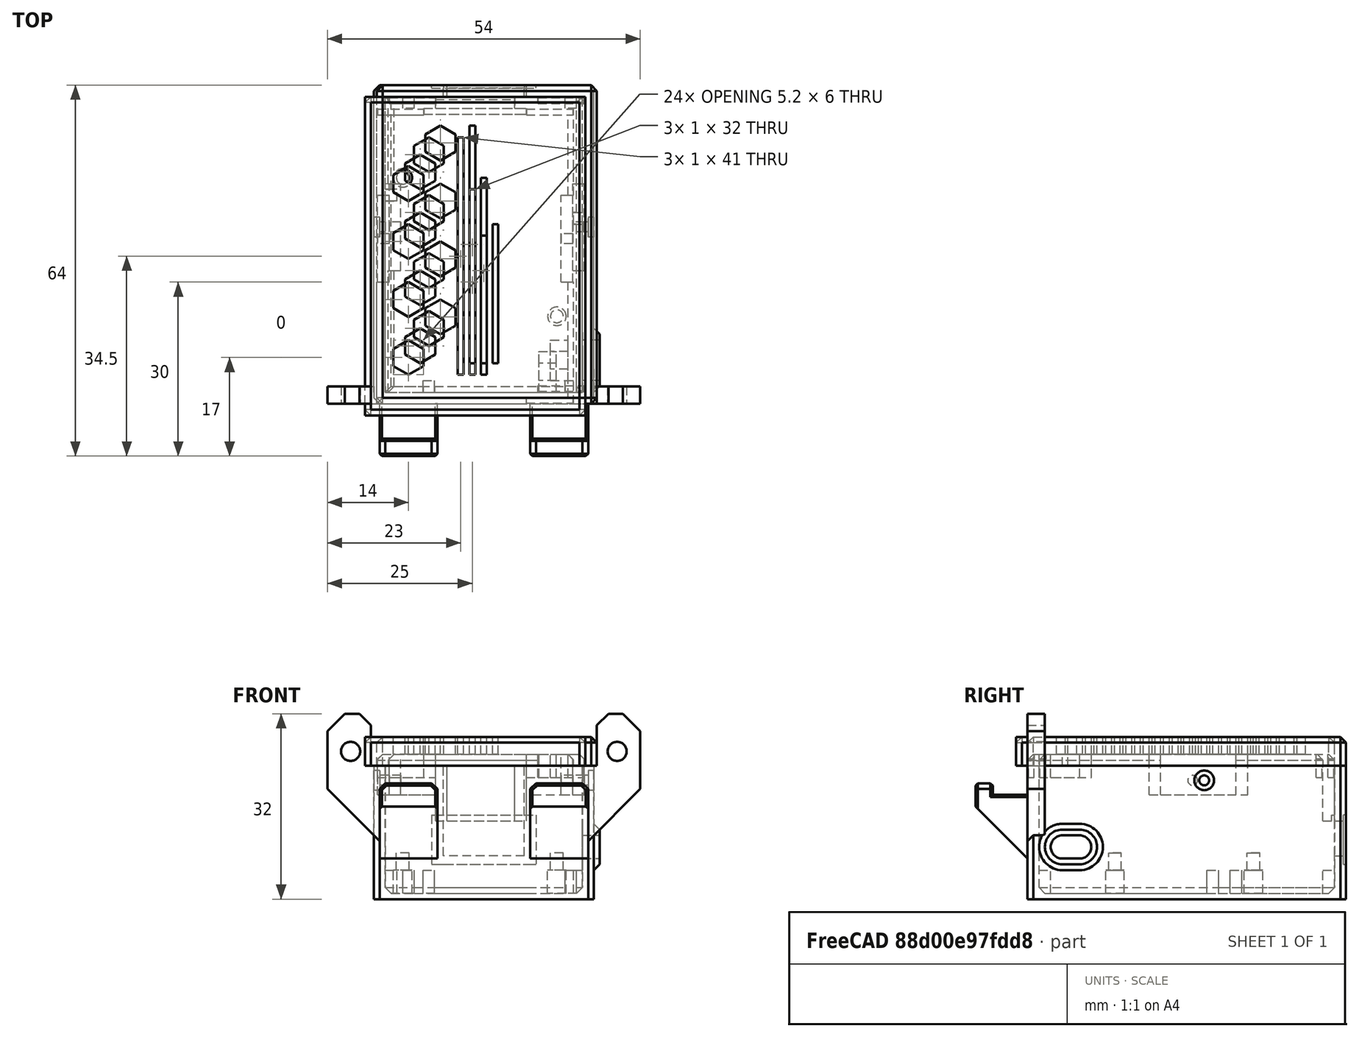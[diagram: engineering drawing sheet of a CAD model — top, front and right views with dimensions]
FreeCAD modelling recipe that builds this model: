
FCSTD DOCUMENT  (FreeCAD 0.18R16146 (Git))
Label: ac-dc5v-adapter
License: All rights reserved
LicenseURL: http://en.wikipedia.org/wiki/All_rights_reserved
objects: Part::Box×43, Part::MultiFuse×24, Part::Cylinder×15, Part::Chamfer×13, Part::Cut×12, Part::Feature×12
note: 119 computed .brp shape members not serialized (recipe doc carries the construction recipe); baked Part::Feature solids carry a one-line shape summary decoded from their .brp

FEATURE [Part::Box] Box  label="Cube"
  AttacherType = Attacher::AttachEngine3D
  Height = 1
  Length = 34
  Width = 51
FEATURE [Part::Box] Box001  label="Cube001"
  AttacherType = Attacher::AttachEngine3D
  Height = 5
  Length = 2
  Placement = pos=(6.5,0,0) rot=(0,0,1;0rad)
  Width = 2
FEATURE [Part::Box] Box002  label="Cube002"
  AttacherType = Attacher::AttachEngine3D
  Height = 5
  Length = 2
  Placement = pos=(0,33,0) rot=(0,0,1;0rad)
  Width = 2
FEATURE [Part::Box] Box003  label="Cube003"
  AttacherType = Attacher::AttachEngine3D
  Height = 5
  Length = 2
  Placement = pos=(31,0,0) rot=(0,0,1;0rad)
  Width = 2
FEATURE [Part::Box] Box004  label="Cube004"
  AttacherType = Attacher::AttachEngine3D
  Height = 5
  Length = 2
  Placement = pos=(31,49,0) rot=(0,0,1;0rad)
  Width = 2
FEATURE [Part::Box] Box005  label="Cube005"
  AttacherType = Attacher::AttachEngine3D
  Height = 5
  Length = 2
  Placement = pos=(3,49,0) rot=(0,0,1;0rad)
  Width = 2
FEATURE [Part::Box] Box006  label="Cube006"
  AttacherType = Attacher::AttachEngine3D
  Height = 5
  Length = 1.5
  Placement = pos=(32.5,29,0) rot=(0,0,1;0rad)
  Width = 2
FEATURE [Part::Box] Box007  label="Cube007"
  AttacherType = Attacher::AttachEngine3D
  Height = 23
  Length = 2
  Placement = pos=(-2,-2,0) rot=(0,0,1;0rad)
  Width = 55
FEATURE [Part::MultiFuse] Fusion
  Shapes = -> [Box006,Box005,Box004,Box003,Box002,Box001]
FEATURE [Part::Box] Box008  label="Cube008"
  AttacherType = Attacher::AttachEngine3D
  Height = 23
  Length = 38
  Placement = pos=(-2,-2,0) rot=(0,0,1;0rad)
  Width = 2
FEATURE [Part::Box] Box009  label="Cube009"
  AttacherType = Attacher::AttachEngine3D
  Height = 23
  Length = 12
  Placement = pos=(-2,51,0) rot=(0,0,1;0rad)
  Width = 2
FEATURE [Part::Box] Box010  label="Cube010"
  AttacherType = Attacher::AttachEngine3D
  Height = 23
  Length = 2
  Placement = pos=(34,-2,0) rot=(0,0,1;0rad)
  Width = 55
FEATURE [Part::Cylinder] Cylinder
  Angle = 360
  AttacherType = Attacher::AttachEngine3D
  Height = 5
  Placement = pos=(3,37,0) rot=(0,0,1;0rad)
  Radius = 1.6
FEATURE [Part::Cylinder] Cylinder001
  Angle = 360
  AttacherType = Attacher::AttachEngine3D
  Height = 5
  Placement = pos=(29.6,13.1,0) rot=(0,0,1;0rad)
  Radius = 1.6
FEATURE [Part::Cylinder] Cylinder002
  Angle = 360
  AttacherType = Attacher::AttachEngine3D
  Height = 8
  Placement = pos=(29.6,13.1,0) rot=(0,0,1;0rad)
  Radius = 1.1
FEATURE [Part::Cylinder] Cylinder003
  Angle = 360
  AttacherType = Attacher::AttachEngine3D
  Height = 8
  Placement = pos=(3,37,0) rot=(0,0,1;0rad)
  Radius = 1.1
FEATURE [Part::Box] Box011  label="Cube011"
  AttacherType = Attacher::AttachEngine3D
  Height = 23
  Length = 12
  Placement = pos=(24,51,0) rot=(0,0,1;0rad)
  Width = 2
FEATURE [Part::Box] Box012  label="Cube012"
  AttacherType = Attacher::AttachEngine3D
  Height = 7.5
  Length = 15
  Placement = pos=(9.5,51,0) rot=(0,0,1;0rad)
  Width = 2
FEATURE [Part::Box] Box013  label="Cube013"
  AttacherType = Attacher::AttachEngine3D
  Height = 8.5
  Length = 18
  Placement = pos=(8,52.5,6) rot=(0,0,1;0rad)
  Width = 2
FEATURE [Part::Box] Box014  label="Cube014"
  AttacherType = Attacher::AttachEngine3D
  Height = 2
  Length = 8
  Placement = pos=(0.15,49.85,25) rot=(0,0,1;0rad)
  Width = 1
FEATURE [Part::Box] Box015  label="Cube015"
  AttacherType = Attacher::AttachEngine3D
  Height = 2
  Length = 8
  Placement = pos=(25.85,49.85,25) rot=(0,0,1;0rad)
  Width = 1
FEATURE [Part::Box] Box016  label="Cube016"
  AttacherType = Attacher::AttachEngine3D
  Height = 5
  Length = 2
  Placement = pos=(0.15,21,22) rot=(0,0,1;0rad)
  Width = 15
FEATURE [Part::Box] Box017  label="Cube017"
  AttacherType = Attacher::AttachEngine3D
  Height = 5
  Length = 2
  Placement = pos=(31.85,21,22) rot=(0,0,1;0rad)
  Width = 15
FEATURE [Part::Box] Box018  label="Cube018"
  AttacherType = Attacher::AttachEngine3D
  Height = 2
  Length = 8
  Placement = pos=(25.85,0.15,25) rot=(0,0,1;0rad)
  Width = 1
FEATURE [Part::Box] Box020  label="Cube020"
  AttacherType = Attacher::AttachEngine3D
  Height = 11.5
  Length = 13.7
  Placement = pos=(10.15,51,13.5) rot=(0,0,1;0rad)
  Width = 2
FEATURE [Part::Box] Box021  label="Cube021"
  AttacherType = Attacher::AttachEngine3D
  Height = 1
  Length = 13.7
  Placement = pos=(10.15,52.5,13.5) rot=(0,0,1;0rad)
  Width = 0.5
FEATURE [Part::Cut] Cut001
  Base = -> Box020
  Placement = pos=(0,0,2) rot=(0,0,1;0rad)
  Tool = -> Box021
FEATURE [Part::MultiFuse] Fusion009
  Shapes = -> [Box011,Box009,Box010,Box007,Box008]
FEATURE [Part::MultiFuse] Fusion010
  Shapes = -> [Box012,Box,Fusion009]
FEATURE [Part::Cut] Cut
  Base = -> Fusion010
  Tool = -> Box013
FEATURE [Part::Chamfer] Chamfer
  Base = -> Cut
  Edges = 4 edges r=1: [Edge5,Edge9,Edge10,Edge11]
FEATURE [Part::Box] Box022  label="Cube022"
  AttacherType = Attacher::AttachEngine3D
  Height = 2
  Length = 2
  Placement = pos=(-2,-2,0) rot=(0,0,1;0rad)
  Width = 55
FEATURE [Part::Box] Box023  label="Cube023"
  AttacherType = Attacher::AttachEngine3D
  Height = 2
  Length = 2
  Placement = pos=(34,-2,0) rot=(0,0,1;0rad)
  Width = 55
FEATURE [Part::Box] Box024  label="Cube024"
  AttacherType = Attacher::AttachEngine3D
  Height = 2
  Length = 38
  Placement = pos=(-2,-2,0) rot=(0,0,1;0rad)
  Width = 2
FEATURE [Part::Box] Box025  label="Cube025"
  AttacherType = Attacher::AttachEngine3D
  Height = 2
  Length = 38
  Placement = pos=(-2,51,0) rot=(0,0,1;0rad)
  Width = 2
FEATURE [Part::MultiFuse] Fusion012
  Placement = pos=(0,0,25) rot=(0,0,1;0rad)
  Shapes = -> [Box025,Box024,Box023,Box022]
FEATURE [Part::Box] Box026  label="Cube026"
  AttacherType = Attacher::AttachEngine3D
  Height = 3
  Length = 38
  Placement = pos=(-2,-2,27) rot=(0,0,1;0rad)
  Width = 55
FEATURE [Part::MultiFuse] Fusion013
  Shapes = -> [Cut001,Box026,Fusion012]
FEATURE [Part::Box] Box027  label="Cube027"
  AttacherType = Attacher::AttachEngine3D
  Height = 2
  Length = 8
  Placement = pos=(25.85,0,25) rot=(0,0,1;0rad)
  Width = 1.15
FEATURE [Part::Box] Box028  label="Cube028"
  AttacherType = Attacher::AttachEngine3D
  Height = 2
  Length = 2.15
  Placement = pos=(0,21,25) rot=(0,0,1;0rad)
  Width = 15
FEATURE [Part::Box] Box029  label="Cube029"
  AttacherType = Attacher::AttachEngine3D
  Height = 2
  Length = 8
  Placement = pos=(25.85,49.85,25) rot=(0,0,1;0rad)
  Width = 1.15
FEATURE [Part::Box] Box030  label="Cube030"
  AttacherType = Attacher::AttachEngine3D
  Height = 2
  Length = 2.15
  Placement = pos=(31.85,21,25) rot=(0,0,1;0rad)
  Width = 15
FEATURE [Part::Box] Box031  label="Cube031"
  AttacherType = Attacher::AttachEngine3D
  Height = 2
  Length = 8
  Placement = pos=(0.15,49.85,25) rot=(0,0,1;0rad)
  Width = 1.15
FEATURE [Part::MultiFuse] Fusion014
  Shapes = -> [Box031,Box030,Box029,Box028,Box027]
FEATURE [Part::MultiFuse] Fusion016
  Placement = pos=(0,0,-2) rot=(0,0,1;0rad)
  Shapes = -> [Box018,Box016,Box015,Box017,Box014]
FEATURE [Part::Box] Box032  label="Cube032"
  AttacherType = Attacher::AttachEngine3D
  Height = 4
  Length = 3
  Width = 7
FEATURE [Part::Box] Box033  label="Cube033"
  AttacherType = Attacher::AttachEngine3D
  Height = 4
  Length = 3
  Placement = pos=(0,2,2) rot=(0,0,1;0rad)
  Width = 3
FEATURE [Part::Cut] Cut002
  Base = -> Box032
  Placement = pos=(28,2,23) rot=(0,0,1;0rad)
  Tool = -> Box033
FEATURE [Part::Cylinder] Cylinder004
  Angle = 360
  AttacherType = Attacher::AttachEngine3D
  Height = 10
  Placement = pos=(5,28.5,20.5) rot=(0,-1,0;1.5708rad)
  Radius = 0.85
FEATURE [Part::Cylinder] Cylinder005
  Angle = 360
  AttacherType = Attacher::AttachEngine3D
  Height = 10
  Placement = pos=(38,28.5,20.5) rot=(0,-1,0;1.5708rad)
  Radius = 0.85
FEATURE [Part::Cylinder] Cylinder006
  Angle = 360
  AttacherType = Attacher::AttachEngine3D
  Height = 1
  Placement = pos=(36,28.5,20.5) rot=(0,-1,0;1.5708rad)
  Radius = 1.7
FEATURE [Part::Cylinder] Cylinder007
  Angle = 360
  AttacherType = Attacher::AttachEngine3D
  Height = 1
  Placement = pos=(-1,28.5,20.5) rot=(0,-1,0;1.5708rad)
  Radius = 1.7
FEATURE [Part::MultiFuse] Fusion019
  Shapes = -> [Cylinder005,Cylinder004]
FEATURE [Part::Cylinder] Cylinder008
  Angle = 360
  AttacherType = Attacher::AttachEngine3D
  Height = 10
  Placement = pos=(38,28.5,20.5) rot=(0,-1,0;1.5708rad)
  Radius = 0.85
FEATURE [Part::Cylinder] Cylinder009
  Angle = 360
  AttacherType = Attacher::AttachEngine3D
  Height = 10
  Placement = pos=(5,28.5,20.5) rot=(0,-1,0;1.5708rad)
  Radius = 0.85
FEATURE [Part::MultiFuse] Fusion020
  Shapes = -> [Cylinder009,Cylinder008]
FEATURE [Part::MultiFuse] Fusion021
  Shapes = -> [Cylinder006,Cylinder007]
FEATURE [Part::Feature] Body001
  Placement = pos=(19,8,20) rot=(0,0,-1;1.5708rad)
  shape: bbox 5.196 x 6 x 10 mm, 8 faces (baked)
FEATURE [Part::Feature] Body002001  label="Body003"
  Placement = pos=(3.5,5,0) rot=(0,0,1;0rad)
  shape: bbox 5.196 x 6 x 10 mm, 8 faces (baked)
FEATURE [Part::Feature] Body001001  label="Body004"
  Placement = pos=(0,10,0) rot=(0,0,1;0rad)
  shape: bbox 5.196 x 6 x 10 mm, 8 faces (baked)
FEATURE [Part::Feature] Body002002  label="Body005"
  Placement = pos=(3.5,15,0) rot=(0,0,1;0rad)
  shape: bbox 5.196 x 6 x 10 mm, 8 faces (baked)
FEATURE [Part::Feature] Body002003  label="Body006"
  Placement = pos=(0,20,0) rot=(0,0,1;0rad)
  shape: bbox 5.196 x 6 x 10 mm, 8 faces (baked)
FEATURE [Part::Feature] Body002004  label="Body007"
  Placement = pos=(3.5,25,0) rot=(0,0,1;0rad)
  shape: bbox 5.196 x 6 x 10 mm, 8 faces (baked)
FEATURE [Part::Feature] Body002005  label="Body008"
  Placement = pos=(0,30,0) rot=(0,0,1;0rad)
  shape: bbox 5.196 x 6 x 10 mm, 8 faces (baked)
FEATURE [Part::Feature] Body002006  label="Body009"
  Placement = pos=(3.5,35,0) rot=(0,0,1;0rad)
  shape: bbox 5.196 x 6 x 10 mm, 8 faces (baked)
FEATURE [Part::MultiFuse] Fusion022
  Placement = pos=(-13.5,0,0) rot=(0,0,1;0rad)
  Shapes = -> [Body002006,Body002004,Body002003,Body002005,Body001001,Body002002,Body002001,Body001]
FEATURE [Part::MultiFuse] Fusion023
  Shapes = -> [Fusion016,Fusion014]
FEATURE [Part::Chamfer] Chamfer001
  Base = -> Fusion013
  Edges = 4 edges r=1: [Edge68,Edge72,Edge88,Edge89]
FEATURE [Part::MultiFuse] Fusion024
  Placement = pos=(0,0,-2) rot=(0,0,1;0rad)
  Shapes = -> [Chamfer001,Fusion023,Cut002]
FEATURE [Part::Cut] Cut006
  Base = -> Fusion024
  Tool = -> Fusion020
FEATURE [Part::Cut] Cut007
  Base = -> Cut006
  Tool = -> Fusion022
FEATURE [Part::Box] Box034  label="Cube034"
  AttacherType = Attacher::AttachEngine3D
  Height = 10
  Length = 1
  Placement = pos=(14,5,22) rot=(0,0,1;0rad)
  Width = 41
FEATURE [Part::Box] Box035  label="Cube035"
  AttacherType = Attacher::AttachEngine3D
  Height = 10
  Length = 1
  Placement = pos=(16,5,22) rot=(0,0,1;0rad)
  Width = 32
FEATURE [Part::Box] Box036  label="Cube036"
  AttacherType = Attacher::AttachEngine3D
  Height = 10
  Length = 1
  Placement = pos=(18,5,22) rot=(0,0,1;0rad)
  Width = 24
FEATURE [Part::MultiFuse] Fusion025
  Shapes = -> [Box036,Box035,Box034]
FEATURE [Part::Cut] Cut008
  Base = -> Cut007
  Tool = -> Fusion025
FEATURE [Part::Feature] Cut008001  label="Cut009"
  shape: bbox 38 x 55 x 14.5 mm, 125 faces (baked)
FEATURE [Part::Chamfer] Chamfer002  label="cap"
  Base = -> Cut008001
  Edges = 8 edges r=1: [Edge310,Edge311,Edge312,Edge313,Edge355,Edge356,Edge361,Edge363]
  Placement = pos=(2,2,0) rot=(0,0,1;0rad)
FEATURE [Part::Cylinder] Cylinder010
  Angle = 360
  AttacherType = Attacher::AttachEngine3D
  Height = 3
  Placement = pos=(37,4,19) rot=(0,-1,0;1.5708rad)
  Radius = 4
FEATURE [Part::Cylinder] Cylinder011
  Angle = 360
  AttacherType = Attacher::AttachEngine3D
  Height = 3
  Placement = pos=(37,4,9) rot=(0,-1,0;1.5708rad)
  Radius = 2
FEATURE [Part::Chamfer] Chamfer003
  Base = -> Cylinder010
  Edges = 1 edges r=1: [Edge3]
  Placement = pos=(0,0,-10) rot=(0,0,1;0rad)
FEATURE [Part::Feature] Chamfer002001  label="cap001"
  shape: bbox 38 x 55 x 14.5 mm, 137 faces (baked)
FEATURE [Part::Feature] Chamfer003001  label="Chamfer004"
  Placement = pos=(0,3,-10) rot=(0,0,1;0rad)
  shape: bbox 3 x 8 x 8 mm, 4 faces (baked)
FEATURE [Part::Cylinder] Cylinder012
  Angle = 360
  AttacherType = Attacher::AttachEngine3D
  Height = 3
  Placement = pos=(37,7,9) rot=(0,-1,0;1.5708rad)
  Radius = 2
FEATURE [Part::Box] Box037  label="Cube037"
  AttacherType = Attacher::AttachEngine3D
  Height = 8
  Length = 3
  Placement = pos=(34,4,5) rot=(0,0,1;0rad)
  Width = 3
FEATURE [Part::Chamfer] Chamfer003002
  Base = -> Box037
  Edges = 2 edges r=1: [Edge6,Edge8]
FEATURE [Part::Box] Box038  label="Cube038"
  AttacherType = Attacher::AttachEngine3D
  Height = 4
  Length = 3
  Placement = pos=(34,4,7) rot=(0,0,1;0rad)
  Width = 3
FEATURE [Part::MultiFuse] Fusion026
  Shapes = -> [Chamfer003001,Chamfer003002,Chamfer003]
FEATURE [Part::MultiFuse] Fusion027
  Shapes = -> [Box038,Cylinder012,Cylinder011]
FEATURE [Part::Box] Box040  label="Cube040"
  AttacherType = Attacher::AttachEngine3D
  Height = 22
  Length = 54
  Placement = pos=(-8,0,10) rot=(0,0,1;0rad)
  Width = 3
FEATURE [Part::Chamfer] Chamfer003004
  Base = -> Box040
  Edges = 2 edges r=9: [Edge4,Edge8]
FEATURE [Part::Cylinder] Cylinder013
  Angle = 360
  AttacherType = Attacher::AttachEngine3D
  Height = 10
  Placement = pos=(-4,6e-15,25.5) rot=(1,0,0;1.5708rad)
  Radius = 1.65
FEATURE [Part::Cylinder] Cylinder014
  Angle = 360
  AttacherType = Attacher::AttachEngine3D
  Height = 10
  Placement = pos=(42,6e-15,25.5) rot=(1,0,0;1.5708rad)
  Radius = 1.65
FEATURE [Part::MultiFuse] Fusion032
  Placement = pos=(0,4,0) rot=(0,0,1;0rad)
  Shapes = -> [Cylinder013,Cylinder014]
FEATURE [Part::Chamfer] Chamfer003005
  Base = -> Chamfer003004
  Edges = 2 edges r=3: [Edge3,Edge13]
FEATURE [Part::Cut] Cut008005
  Base = -> Chamfer003005
  Placement = pos=(-0.5,0,0) rot=(0,0,1;0rad)
  Tool = -> Fusion032
FEATURE [Part::Box] Box041  label="Cube041"
  AttacherType = Attacher::AttachEngine3D
  Height = 10
  Length = 39
  Placement = pos=(-1,0,23) rot=(0,0,1;0rad)
  Width = 10
FEATURE [Part::Box] Box042  label="Cube042"
  AttacherType = Attacher::AttachEngine3D
  Height = 11
  Length = 10
  Placement = pos=(1,-9,7) rot=(0,0,1;0rad)
  Width = 10
FEATURE [Part::Chamfer] Chamfer003007
  Base = -> Box042
  Edges = 1 edges r=9: [Edge9]
FEATURE [Part::Box] Box043  label="Cube043"
  AttacherType = Attacher::AttachEngine3D
  Height = 3
  Length = 10
  Placement = pos=(1,-9,17) rot=(0,0,1;0rad)
  Width = 3
FEATURE [Part::Chamfer] Chamfer003008
  Base = -> Box043
  Edges = 2 edges r=1: [Edge2,Edge6]
FEATURE [Part::Chamfer] Chamfer003009
  Base = -> Chamfer003008
  Edges = 12 edges r=0.4: [Edge1,Edge4,Edge5,Edge6,Edge7,Edge8,Edge9,Edge11,Edge12,Edge14,Edge15,Edge16]
FEATURE [Part::Chamfer] Chamfer003010
  Base = -> Chamfer003007
  Edges = 4 edges r=0.4: [Edge1,Edge3,Edge6,Edge12]
FEATURE [Part::MultiFuse] Fusion033
  Placement = pos=(-0.5,0,0) rot=(0,0,1;0rad)
  Shapes = -> [Chamfer003009,Chamfer003010]
FEATURE [Part::Feature] Fusion033001  label="Fusion034"
  Placement = pos=(25.5,0,0) rot=(0,0,1;0rad)
  shape: bbox 10 x 10 x 13 mm, 23 faces (baked)
FEATURE [Part::MultiFuse] Fusion033003
  Shapes = -> [Cylinder003,Cylinder,Cylinder002,Cylinder001]
FEATURE [Part::MultiFuse] Fusion033004
  Shapes = -> [Chamfer,Fusion]
FEATURE [Part::Cut] Cut008007
  Base = -> Fusion033004
  Tool = -> Fusion019
FEATURE [Part::Cut] Cut008008
  Base = -> Cut008007
  Tool = -> Fusion021
FEATURE [Part::MultiFuse] Fusion033005
  Shapes = -> [Fusion026,Cut008008]
FEATURE [Part::Cut] Cut008009
  Base = -> Fusion033005
  Tool = -> Fusion027
FEATURE [Part::MultiFuse] Fusion033006
  Shapes = -> [Cut008009,Fusion033003]
FEATURE [Part::Chamfer] Chamfer003011
  Base = -> Fusion033006
  Edges = 4 edges r=1: [Edge241,Edge244,Edge274,Edge349]
  Placement = pos=(1.5,2,0) rot=(0,0,1;0rad)
FEATURE [Part::Box] Box044  label="Cube044"
  AttacherType = Attacher::AttachEngine3D
  Height = 34
  Length = 34
  Placement = pos=(1.5,2,10) rot=(0,0,1;0rad)
  Width = 5
FEATURE [Part::MultiFuse] Fusion033007
  Shapes = -> [Cut008005,Fusion033,Fusion033001]
FEATURE [Part::Cut] Cut008010
  Base = -> Fusion033007
  Tool = -> Box044
FEATURE [Part::Cut] Cut008011
  Base = -> Cut008010
  Tool = -> Box041
FEATURE [Part::Chamfer] Chamfer003012
  Base = -> Cut008011
  Edges = 2 edges r=2: [Edge93,Edge102]
FEATURE [Part::MultiFuse] Fusion033008
  Shapes = -> [Chamfer003012,Chamfer003011]
